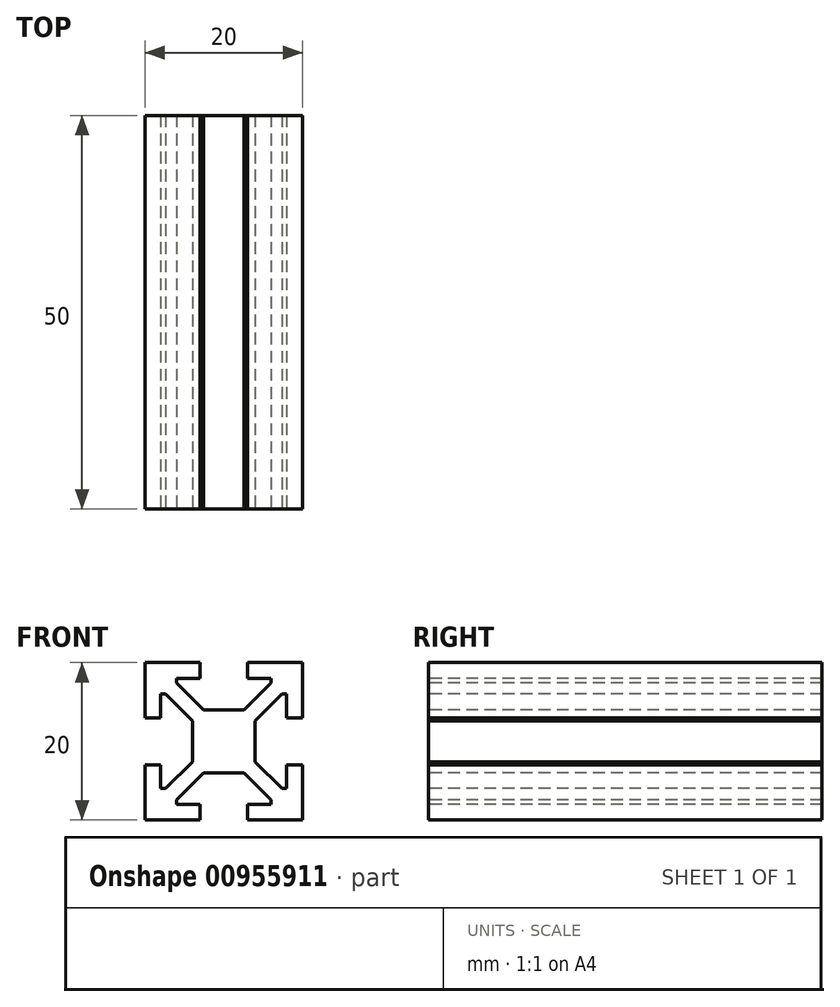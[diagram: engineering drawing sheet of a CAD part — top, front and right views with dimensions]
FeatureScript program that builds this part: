
annotation { "Feature Type Name" : "Feature", "Feature Type Description" : "" }
export const myFeature = defineFeature(function(context is Context, id is Id, definition is map)
    precondition{}
    {
        {
            var Q0;
            Q0=qCreatedBy(makeId("Front.planeOp"),FACE);
            var sketch = newSketch(context, id + "F0", { "sketchPlane" : qUnion([Q0])});
            skLineSegment(sketch, "E0.bottom", {"start": v(10, 10) * mm, "end": v(3, 10) * mm});
            skLineSegment(sketch, "E0.top", {"start": v(10, -10) * mm, "end": v(3, -10) * mm});
            skLineSegment(sketch, "E0.left", {"start": v(10, 10) * mm, "end": v(10, 3) * mm});
            skLineSegment(sketch, "E0.right", {"start": v(-10, 10) * mm, "end": v(-10, 3) * mm});
            skPoint(sketch, "E0.middle", {"position": v(0, 0) * mm});
            skLineSegment(sketch, "E1.bottom", {"start": v(2.59, -4) * mm, "end": v(-2.59, -4) * mm});
            skLineSegment(sketch, "E1.left", {"start": v(4, -2.59) * mm, "end": v(4, 2.59) * mm});
            skLineSegment(sketch, "E1.right", {"start": v(-4, -2.59) * mm, "end": v(-4, 2.59) * mm});
            skLineSegment(sketch, "E2.bottom", {"start": v(6.59, -8) * mm, "end": v(3, -8) * mm});
            skLineSegment(sketch, "E2.top", {"start": v(6.59, 8) * mm, "end": v(3, 8) * mm});
            skLineSegment(sketch, "E2.left", {"start": v(8, -6.59) * mm, "end": v(8, -3) * mm});
            skLineSegment(sketch, "E2.right", {"start": v(-8, -6.59) * mm, "end": v(-8, -3) * mm});
            skLineSegment(sketch, "E3.left", {"start": v(3, -10) * mm, "end": v(3, -8) * mm});
            skLineSegment(sketch, "E3.right", {"start": v(-3, -10) * mm, "end": v(-3, -8) * mm});
            skLineSegment(sketch, "E4.bottom", {"start": v(-10, -3) * mm, "end": v(-8, -3) * mm});
            skLineSegment(sketch, "E4.top", {"start": v(-10, 3) * mm, "end": v(-8, 3) * mm});
            skLineSegment(sketch, "E5.trimOffspring", {"start": v(-3, 10) * mm, "end": v(-10, 10) * mm});
            skLineSegment(sketch, "E6.trimOffspring", {"start": v(-10, -3) * mm, "end": v(-10, -10) * mm});
            skLineSegment(sketch, "E7.trimOffspring", {"start": v(10, -3) * mm, "end": v(10, -10) * mm});
            skLineSegment(sketch, "E8.trimOffspring", {"start": v(-3, -10) * mm, "end": v(-10, -10) * mm});
            skLineSegment(sketch, "E9", {"start": v(0, 0) * mm, "end": v(-10, 10) * mm, "construction": true});
            skLineSegment(sketch, "E10", {"start": v(-6, 7.41) * mm, "end": v(-2.59, 4) * mm});
            skLineSegment(sketch, "E11", {"start": v(-7.41, 6) * mm, "end": v(-4, 2.59) * mm});
            skLineSegment(sketch, "E12.trimOffspring", {"start": v(-3, 8) * mm, "end": v(-3, 10) * mm});
            skLineSegment(sketch, "E13.trimOffspring", {"start": v(8, 3) * mm, "end": v(10, 3) * mm});
            skPoint(sketch, "E14.orphan", {"position": v(-8, 8) * mm});
            skLineSegment(sketch, "E15", {"start": v(0, 0) * mm, "end": v(0, 16.22) * mm, "construction": true});
            skLineSegment(sketch, "E16.MirrorCS", {"start": v(6.59, 8) * mm, "end": v(2.59, 4) * mm});
            skLineSegment(sketch, "E17.MirrorCS", {"start": v(8, 6.59) * mm, "end": v(4, 2.59) * mm});
            skLineSegment(sketch, "E18.trimOffspring", {"start": v(-3, 8) * mm, "end": v(-6, 8) * mm});
            skLineSegment(sketch, "E19.trimOffspring", {"start": v(3, 8) * mm, "end": v(3, 10) * mm});
            skLineSegment(sketch, "E20.trimOffspring", {"start": v(2.59, 4) * mm, "end": v(-2.59, 4) * mm});
            skLineSegment(sketch, "E21", {"start": v(0, 0) * mm, "end": v(-16.72, 0) * mm, "construction": true});
            skLineSegment(sketch, "E22.MirrorCS", {"start": v(-8, -6.59) * mm, "end": v(-4, -2.59) * mm});
            skLineSegment(sketch, "E23.MirrorCS", {"start": v(-6.59, -8) * mm, "end": v(-2.59, -4) * mm});
            skLineSegment(sketch, "E24.MirrorCS", {"start": v(8, -6.59) * mm, "end": v(4, -2.59) * mm});
            skLineSegment(sketch, "E25.MirrorCS", {"start": v(6.59, -8) * mm, "end": v(2.59, -4) * mm});
            skLineSegment(sketch, "E26.trimOffspring", {"start": v(-8, 3) * mm, "end": v(-8, 6) * mm});
            skLineSegment(sketch, "E27.trimOffspring", {"start": v(8, -3) * mm, "end": v(10, -3) * mm});
            skLineSegment(sketch, "E28.trimOffspring", {"start": v(-3, -8) * mm, "end": v(-6.59, -8) * mm});
            skLineSegment(sketch, "E29.trimOffspring", {"start": v(8, 3) * mm, "end": v(8, 6.59) * mm});
            skPoint(sketch, "E30.orphan", {"position": v(8, -8) * mm});
            skPoint(sketch, "E31.orphan", {"position": v(-8, -8) * mm});
            skPoint(sketch, "E32.orphan", {"position": v(8, 8) * mm});
            skPoint(sketch, "E33.startSnap0", {"position": v(-10, 6.5) * mm});
            skLineSegment(sketch, "E34", {"start": v(-6, 8) * mm, "end": v(-6, 7.41) * mm});
            skLineSegment(sketch, "E35", {"start": v(-8, 6) * mm, "end": v(-7.41, 6) * mm});
            skLineSegment(sketch, "E36", {"start": v(0, 0) * mm, "end": v(0, 4) * mm});
            skLineSegment(sketch, "E37", {"start": v(0, 0) * mm, "end": v(-4, 0) * mm});
            skPoint(sketch, "E38.orphan", {"position": v(-6.59, 8) * mm});
            skPoint(sketch, "E39.orphan", {"position": v(-8, 6.59) * mm});
            skSolve(sketch);
        }
        {
            var Q0;
            Q0=makeQuery(id+"F0.imprint","IMPRINT",FACE,{"disambiguationData":[TD([[makeQuery(id+"F0.imprint","IMPRINT",EDGE,{"derivedFrom":sQuery(id+"F0.wireOp",EDGE,"E0.right")}),1.0]])]});
            extrude(context, id + "F1", {"entities" : qUnion([Q0]), "oppositeDirection" : true, "depth" : 50 * mm, "offsetDistance" : 25 * mm});
        }
        {
            var Q0;
            Q0=makeQuery(id+"F1.opExtrude","SWEPT_BODY",BODY,{"disambiguationData":[OSD([sQuery(id+"F0.wireOp",EDGE,"E0.right"),sQuery(id+"F0.wireOp",EDGE,"E1.right"),sQuery(id+"F0.wireOp",EDGE,"E4.top"),sQuery(id+"F0.wireOp",EDGE,"E5.trimOffspring"),sQuery(id+"F0.wireOp",EDGE,"E10"),sQuery(id+"F0.wireOp",EDGE,"E11"),sQuery(id+"F0.wireOp",EDGE,"E12.trimOffspring"),sQuery(id+"F0.wireOp",EDGE,"E18.trimOffspring"),sQuery(id+"F0.wireOp",EDGE,"E20.trimOffspring"),sQuery(id+"F0.wireOp",EDGE,"E26.trimOffspring"),sQuery(id+"F0.wireOp",EDGE,"E34"),sQuery(id+"F0.wireOp",EDGE,"E35"),sQuery(id+"F0.wireOp",EDGE,"E36"),sQuery(id+"F0.wireOp",EDGE,"E37")])]});
            var Q1;
            Q1=makeQuery(id+"F1.opExtrude","SWEPT_FACE",FACE,{"disambiguationData":[OSD([sQuery(id+"F0.wireOp",EDGE,"E36")])]});
            mirror(context, id + "F2", {"operationType" : NewBodyOperationType.ADD, "entities" : qUnion([Q0]), "mirrorPlane" : qUnion([Q1])});
        }
        {
            var Q0;
            Q0=makeQuery(id+"F1.opExtrude","SWEPT_BODY",BODY,{"disambiguationData":[OSD([sQuery(id+"F0.wireOp",EDGE,"E0.right"),sQuery(id+"F0.wireOp",EDGE,"E1.right"),sQuery(id+"F0.wireOp",EDGE,"E4.top"),sQuery(id+"F0.wireOp",EDGE,"E5.trimOffspring"),sQuery(id+"F0.wireOp",EDGE,"E10"),sQuery(id+"F0.wireOp",EDGE,"E11"),sQuery(id+"F0.wireOp",EDGE,"E12.trimOffspring"),sQuery(id+"F0.wireOp",EDGE,"E18.trimOffspring"),sQuery(id+"F0.wireOp",EDGE,"E20.trimOffspring"),sQuery(id+"F0.wireOp",EDGE,"E26.trimOffspring"),sQuery(id+"F0.wireOp",EDGE,"E34"),sQuery(id+"F0.wireOp",EDGE,"E35"),sQuery(id+"F0.wireOp",EDGE,"E36"),sQuery(id+"F0.wireOp",EDGE,"E37")])]});
            var Q1;
            {var subQ0=makeQuery(id+"F1.opExtrude","SWEPT_FACE",FACE,{"disambiguationData":[OSD([sQuery(id+"F0.wireOp",EDGE,"E37")])]});Q1=makeQuery(id+"F2.boolean.opBoolean","MERGE",FACE,{"derivedFrom":[subQ0,makeQuery(id+"F2.opPattern","COPY",FACE,{"derivedFrom":subQ0,"instanceName":"1"})]});}
            mirror(context, id + "F3", {"operationType" : NewBodyOperationType.ADD, "entities" : qUnion([Q0]), "mirrorPlane" : qUnion([Q1])});
        }
    });
